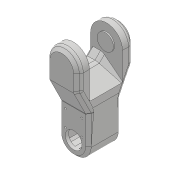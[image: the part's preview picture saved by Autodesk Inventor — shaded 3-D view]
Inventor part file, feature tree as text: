
AUTODESK INVENTOR PART (.ipt)
format: ipt  version: 2018 (Build 220112000, 112)  size: 800,768 bytes
history: native  units: mm
features: sketch x31, projected_geometry x30, extrude x29, chamfer x11, fillet x7, hole x3, mirror x1
ambient origin geometry x8: Origin, YZ Plane, XZ Plane, XY Plane, X Axis, Y Axis, Z Axis, Center Point
bodies: Solid1 (feature_tree)
feature tree (112):
  extrude  "Extrusion1"  Depth=45.0mm
  extrude  "Extrusion2"  Depth=2.25mm
  hole  "Hole1"  [1 undecoded]
  hole  "Hole2"  [1 undecoded]
  fillet  "Fillet1"  Radius=14.0mm
  extrude  "Extrusion3"  Depth=18.5mm
  extrude  "Extrusion4"  Depth=10.0mm
  extrude  "Extrusion5"  Depth=2.195mm
  extrude  "Extrusion6"  Depth=20.5mm
  hole  "Hole3"  [1 undecoded]
  extrude  "Extrusion7"  Depth=0.5mm
  extrude  "Extrusion8"  Depth=5.0mm TaperAngle=0.0deg
  extrude  "Extrusion9"  Depth=10.0mm
  extrude  "Extrusion10"  Depth=10.0mm
  extrude  "Extrusion11"  Depth=14.5mm
  extrude  "Extrusion12"  Depth=14.5mm
  extrude  "Extrusion13"  Depth=5.0mm
  extrude  "Extrusion14"  Depth=2.25mm
  extrude  "Extrusion15"  Depth=5.0mm
  extrude  "Extrusion16"  Depth=9.0mm
  extrude  "Extrusion17"  Depth=14.75mm
  chamfer  "Chamfer1"  Distance=1.0mm
  fillet  "Fillet7"  Radius=20.7mm
  fillet  "Fillet8"  Radius=32.0mm
  mirror  "Mirror1"
  extrude  "Extrusion19"  Depth=1.0mm TaperAngle=0.0deg
  extrude  "Extrusion20"  Depth=8.0mm
  extrude  "Extrusion21"  Depth=0.2mm TaperAngle=0.0deg
  extrude  "Extrusion22"  Depth=0.5mm TaperAngle=0.0deg
  extrude  "Extrusion23"  Depth=9.0mm TaperAngle=0.0deg
  extrude  "Extrusion24"  Depth=0.2mm TaperAngle=0.0deg
  chamfer  "Chamfer2"  Distance=0.2mm
  chamfer  "Chamfer8"  Distance=2.5mm Angle=45.0deg
  extrude  "Extrusion25"  Depth=0.5mm
  extrude  "Extrusion26"  Depth=10.0mm TaperAngle=0.0deg
  chamfer  "Chamfer3"  Distance=40.0mm
  chamfer  "Chamfer4"  Distance=2.0mm
  chamfer  "Chamfer5"  Distance=2.0mm
  chamfer  "Chamfer6"  Distance=40.0mm
  fillet  "Fillet9"  Radius=70.0mm
  fillet  "Fillet10"  Radius=15.0mm
  extrude  "Extrusion27"  Depth=10.0mm TaperAngle=0.0deg
  extrude  "Extrusion28"  Depth=10.0mm TaperAngle=45.0deg
  extrude  "Extrusion29"  Depth=41.6mm
  chamfer  "Chamfer7"  Distance=41.0mm
  extrude  "Extrusion30"  Depth=10.0mm
  fillet  "Fillet18"  Radius=7.0mm
  chamfer  "Chamfer9"  Distance=7.0mm
  chamfer  "Chamfer10"  Distance=100.0mm
  chamfer  "Chamfer11"  Distance=15.282752mm
  fillet  "Fillet19"  Radius=100.0mm
  sketch  "Sketch1"  dims[d0=24.5mm d1=45.0mm]
  sketch  "Sketch2"  dims[d2=1.95mm d3=0.0mm d4=2.25mm]
  projected_geometry  "Projected Loop1"
  sketch  "Sketch3"  dims[d5=20.0mm d6=2.25mm]
  projected_geometry  "Projected Loop2"
  sketch  "Sketch4"  dims[d7=5.25mm d8=5.25mm d9=14.0mm]
  projected_geometry  "Projected Loop3"
  sketch  "Sketch5"  dims[d10=5.25mm d11=18.5mm]
  projected_geometry  "Projected Loop4"
  sketch  "Sketch6"  dims[d12=10.0mm d13=0.0mm d14=20.5mm]
  projected_geometry  "Projected Loop5"
  sketch  "Sketch7"  dims[d15=2.0mm d16=2.195mm]
  projected_geometry  "Projected Loop6"
  sketch  "Sketch8"  dims[d17=2.0mm]
  projected_geometry  "Projected Loop7"
  sketch  "Sketch9"  dims[d18=2.4mm d19=6.0mm d20=4.4mm d21=2.0mm d22=90.0deg d23=8.0mm d24=20.594885mm d25=20.5mm]
  projected_geometry  "Projected Loop8"
  projected_geometry  "Projected Loop9"
  sketch  "Sketch10"  dims[d26=26.65mm d27=2.0mm]
  projected_geometry  "Projected Loop10"
  projected_geometry  "Projected Loop11"
  sketch  "Sketch11"  dims[d28=2.0mm]
  projected_geometry  "Projected Loop12"
  sketch  "Sketch12"  dims[d29=2.4mm d30=6.0mm d31=4.4mm d32=2.0mm d33=90.0deg d34=8.0mm d35=20.594885mm d36=0.5mm]
  sketch  "Sketch13"  dims[d37=18.0mm d38=5.0mm d39=0.0mm]
  sketch  "Sketch14"  dims[d41=10.0mm d42=0.0mm d43=24.5mm]
  projected_geometry  "Projected Loop13"
  sketch  "Sketch15"  dims[d44=1.15mm d45=0.0mm d46=10.0mm]
  sketch  "Sketch16"  dims[d47=21.0mm d48=14.5mm]
  projected_geometry  "Projected Loop14"
  sketch  "Sketch17"  dims[d49=20.0mm d50=14.5mm]
  projected_geometry  "Projected Loop15"
  sketch  "Sketch18"  dims[d51=24.5mm d52=5.0mm]
  projected_geometry  "Projected Loop16"
  sketch  "Sketch19"  dims[d53=5.0mm d54=2.25mm]
  projected_geometry  "Projected Loop17"
  sketch  "Sketch20"  dims[d55=2.25mm d56=5.0mm]
  projected_geometry  "Projected Loop18"
  sketch  "Sketch25"  dims[d57=5.0mm d58=9.0mm]
  projected_geometry  "Projected Loop22"
  sketch  "Sketch26"  dims[d59=14.75mm d60=4.0mm d61=1.0mm d62=0.0mm d63=20.7mm]
  projected_geometry  "Projected Loop23"
  sketch  "Sketch27"  dims[d64=2.4mm d65=6.0mm d66=4.4mm d67=2.0mm d68=90.0deg d69=8.0mm d70=20.594885mm d72=32.0mm]
  projected_geometry  "Projected Loop24"
  sketch  "Sketch28"  dims[d73=5.0mm d74=0.0mm d75=1.0mm d76=0.0mm]
  projected_geometry  "Projected Loop25"
  sketch  "Sketch29"  dims[d77=12.25mm d78=0.0mm d80=8.0mm]
  projected_geometry  "Projected Loop26"
  sketch  "Sketch30"  dims[d81=4.5mm d82=0.0mm d84=0.2mm d85=0.0mm]
  projected_geometry  "Projected Loop27"
  sketch  "Sketch31"  dims[d86=21.0mm d87=0.5mm d88=0.0mm]
  sketch  "Sketch35"  dims[d91=8.0mm d92=0.0mm d93=9.0mm d94=0.0mm]
  projected_geometry  "Projected Loop33"
  sketch  "Sketch36"  dims[d95=5.0mm d96=0.0mm d98=0.2mm d99=0.0mm d100=0.2mm d101=0.0mm d102=2.5mm d103=2.0mm d104=45.0deg]
  projected_geometry  "Projected Loop34"
  sketch  "Sketch38"  dims[d105=1.5mm d114=0.5mm]
  projected_geometry  "Projected Loop36"
  sketch  "Sketch39"  dims[d128=2.0mm d129=0.0mm d130=2.0mm d131=0.0mm d132=40.0mm d133=2.0mm d134=0.0mm d135=2.0mm d136=0.0mm d137=40.0mm d138=70.0mm d139=15.0mm d140=0.0mm d141=56.1mm d142=0.0mm d143=4.0mm d144=8.0mm d145=45.0deg d146=41.6mm d147=41.0mm d148=7.0mm d149=7.0mm d150=7.0mm d151=100.0mm d152=0.0mm d153=15.282752mm d156=100.0mm d157=0.0mm d158=3.0mm d159=2.0mm d160=45.0deg d161=5.0mm d162=2.0mm d163=45.0deg d164=5.0mm d165=2.0mm d166=45.0deg d167=5.0mm d168=2.0mm d169=45.0deg d170=5.0mm d171=2.0mm d188=20.5mm d189=1.6mm d190=0.0mm d191=20.5mm d192=3.1mm d193=0.0mm d202=16.0mm d203=3.1mm d204=0.0mm d205=1.5mm d206=2.0mm d207=45.0deg d209=37.0mm d210=10.0mm d211=0.0mm d231=4.0mm d232=8.0mm d233=45.0deg d234=10.0mm d243=14.0mm d244=25.0mm d245=45.0deg d246=14.0mm d247=25.0mm d248=45.0deg d249=14.0mm d250=25.0mm d251=45.0deg d252=10.0mm]
  projected_geometry  "Projected Loop37"
  projected_geometry  "Project Cut Edges1"
  projected_geometry  "Project Cut Edges2"
note: 3 required parameter values undecoded (feature->parameter linkage not recoverable at this tier; creation-order binding heuristic only, values carry confidence <= 0.55)
